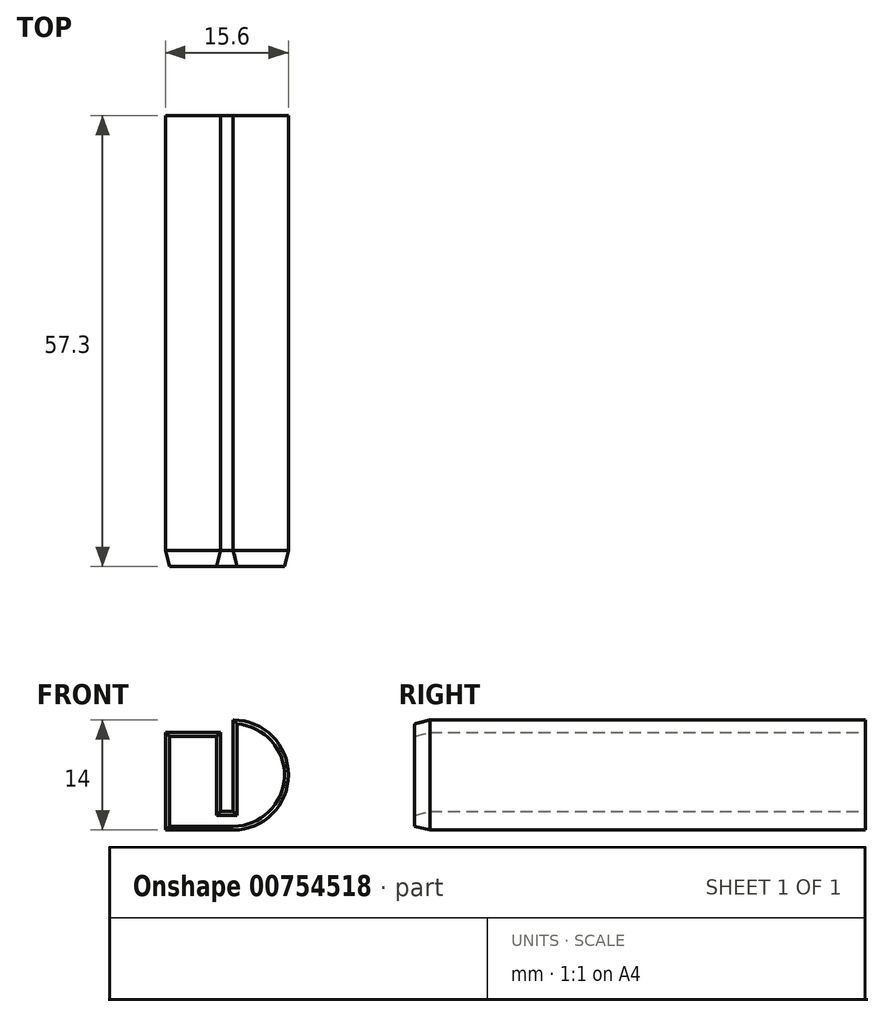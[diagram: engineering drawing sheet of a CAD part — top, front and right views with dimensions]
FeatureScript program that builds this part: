
annotation { "Feature Type Name" : "Feature", "Feature Type Description" : "" }
export const myFeature = defineFeature(function(context is Context, id is Id, definition is map)
    precondition{}
    {
        {
            var Q0;
            Q0=qCreatedBy(makeId("Front.planeOp"),FACE);
            var sketch = newSketch(context, id + "F0", { "sketchPlane" : qUnion([Q0])});
            skLineSegment(sketch, "E0", {"start": v(0, 0) * mm, "end": v(0, 12.4) * mm});
            skLineSegment(sketch, "E1", {"start": v(0, 12.4) * mm, "end": v(7, 12.4) * mm});
            skLineSegment(sketch, "E2", {"start": v(7, 12.4) * mm, "end": v(7, 2.4) * mm});
            skLineSegment(sketch, "E3", {"start": v(7, 2.4) * mm, "end": v(8.6, 2.4) * mm});
            skLineSegment(sketch, "E4", {"start": v(8.6, 2.4) * mm, "end": v(8.6, 14) * mm});
            skLineSegment(sketch, "E5", {"start": v(0, 0) * mm, "end": v(8.6, 0) * mm});
            skArc(sketch, "E6", {"start": v(8.6, 0) * mm, "mid": v(15.6, 7) * mm, "end": v(8.6, 14) * mm});
            skSolve(sketch);
        }
        {
            var Q0;
            Q0=makeQuery(id+"F0.imprint","IMPRINT",FACE,{"disambiguationData":[TD([[makeQuery(id+"F0.imprint","IMPRINT",EDGE,{"derivedFrom":sQuery(id+"F0.wireOp",EDGE,"E0")}),-1.0]])]});
            extrude(context, id + "F1", {"entities" : qUnion([Q0]), "depth" : 57.3 * mm, "offsetDistance" : 25 * mm});
        }
        {
            var Q0;
            Q0=makeQuery(id+"F1.opExtrude","CAP_FACE",FACE,{"disambiguationData":[OSD([sQuery(id+"F0.wireOp",EDGE,"E0"),sQuery(id+"F0.wireOp",EDGE,"E1"),sQuery(id+"F0.wireOp",EDGE,"E2"),sQuery(id+"F0.wireOp",EDGE,"E3"),sQuery(id+"F0.wireOp",EDGE,"E4"),sQuery(id+"F0.wireOp",EDGE,"E5"),sQuery(id+"F0.wireOp",EDGE,"E6")])],"isStart":false});
            chamfer(context, id + "F2", {"entities" : qUnion([Q0]), "chamferType" : ChamferType.TWO_OFFSETS, "width1" : 2 * mm, "oppositeDirection" : false, "width2" : 0.5 * mm, "tangentPropagation" : true});
        }
    });
